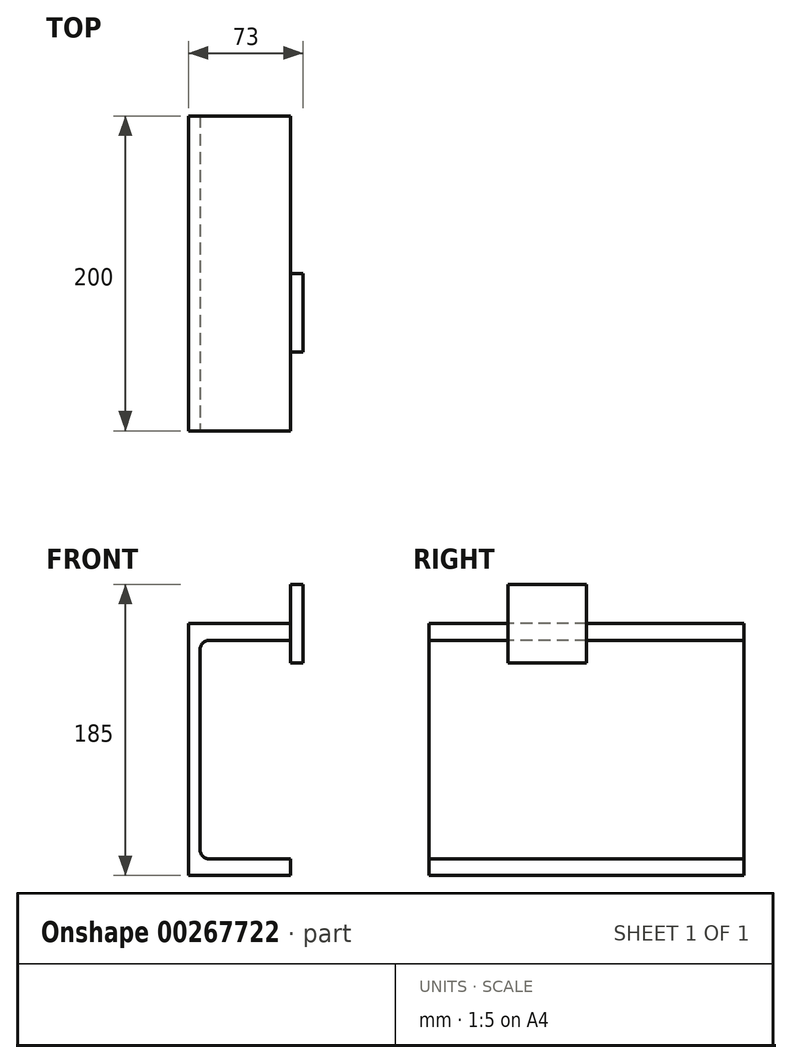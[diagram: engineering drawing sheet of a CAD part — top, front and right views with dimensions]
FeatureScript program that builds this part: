
annotation { "Feature Type Name" : "Feature", "Feature Type Description" : "" }
export const myFeature = defineFeature(function(context is Context, id is Id, definition is map)
    precondition{}
    {
        {
            var Q0;
            Q0=qCreatedBy(makeId("Front.planeOp"),FACE);
            var sketch = newSketch(context, id + "F0", { "sketchPlane" : qUnion([Q0])});
            skLineSegment(sketch, "E0.bottom", {"start": v(32.5, 80) * mm, "end": v(-32.5, 80) * mm});
            skLineSegment(sketch, "E0.top", {"start": v(32.5, -80) * mm, "end": v(-32.5, -80) * mm});
            skLineSegment(sketch, "E0.left", {"start": v(32.5, 80) * mm, "end": v(32.5, 69.5) * mm});
            skLineSegment(sketch, "E0.right", {"start": v(-32.5, 80) * mm, "end": v(-32.5, -80) * mm});
            skPoint(sketch, "E0.middle", {"position": v(0, 0) * mm});
            skLineSegment(sketch, "E1.0", {"start": v(32.5, 69.5) * mm, "end": v(-19, 69.5) * mm});
            skLineSegment(sketch, "E2.0", {"start": v(32.5, -69.5) * mm, "end": v(-19, -69.5) * mm});
            skLineSegment(sketch, "E3.0", {"start": v(-25, 63.5) * mm, "end": v(-25, -63.5) * mm});
            skArc(sketch, "E4.filletArc", {"start": v(-19, 69.5) * mm, "mid": v(-23.24, 67.74) * mm, "end": v(-25, 63.5) * mm});
            skArc(sketch, "E5.filletArc", {"start": v(-25, -63.5) * mm, "mid": v(-23.24, -67.74) * mm, "end": v(-19, -69.5) * mm});
            skLineSegment(sketch, "E6.trimOffspring", {"start": v(32.5, -69.5) * mm, "end": v(32.5, -80) * mm});
            skSolve(sketch);
        }
        {
            var Q0;
            {var subQ3=sQuery(id+"F0.wireOp",EDGE,"E0.bottom");Q0=makeQuery(id+"F0.imprint","IMPRINT",FACE,{"disambiguationData":[TD([[makeQuery(id+"F0.imprint","IMPRINT",EDGE,{"derivedFrom":subQ3}),1.0]])]});}
            extrude(context, id + "F1", {"entities" : qUnion([Q0]), "oppositeDirection" : true, "depth" : 200 * mm});
        }
        {
            var Q0;
            Q0=makeQuery(id+"F1.opExtrude","SWEPT_FACE",FACE,{"disambiguationData":[OSD([sQuery(id+"F0.wireOp",EDGE,"E0.bottom")])]});
            cPlane(context, id + "F2", {"entities" : qUnion([Q0]), "cplaneType" : CPlaneType.OFFSET, "offset" : 25 * mm, "width" : 150 * mm, "height" : 150 * mm});
        }
        {
            var Q0;
            Q0=qCreatedBy(id+"F2.planeOp",FACE);
            var sketch = newSketch(context, id + "F3", { "sketchPlane" : qUnion([Q0])});
            skLineSegment(sketch, "E7.bottom", {"start": v(32.5, 50) * mm, "end": v(40.5, 50) * mm});
            skLineSegment(sketch, "E7.top", {"start": v(32.5, 100) * mm, "end": v(40.5, 100) * mm});
            skLineSegment(sketch, "E7.left", {"start": v(32.5, 50) * mm, "end": v(32.5, 100) * mm});
            skLineSegment(sketch, "E7.right", {"start": v(40.5, 50) * mm, "end": v(40.5, 100) * mm});
            skSolve(sketch);
        }
        {
            var Q0;
            Q0=makeQuery(id+"F3.imprint","IMPRINT",FACE,{"disambiguationData":[TD([[makeQuery(id+"F3.imprint","IMPRINT",EDGE,{"derivedFrom":sQuery(id+"F3.wireOp",EDGE,"E7.bottom")}),1.0]])]});
            extrude(context, id + "F4", {"entities" : qUnion([Q0]), "oppositeDirection" : true, "depth" : 50 * mm});
        }
    });
